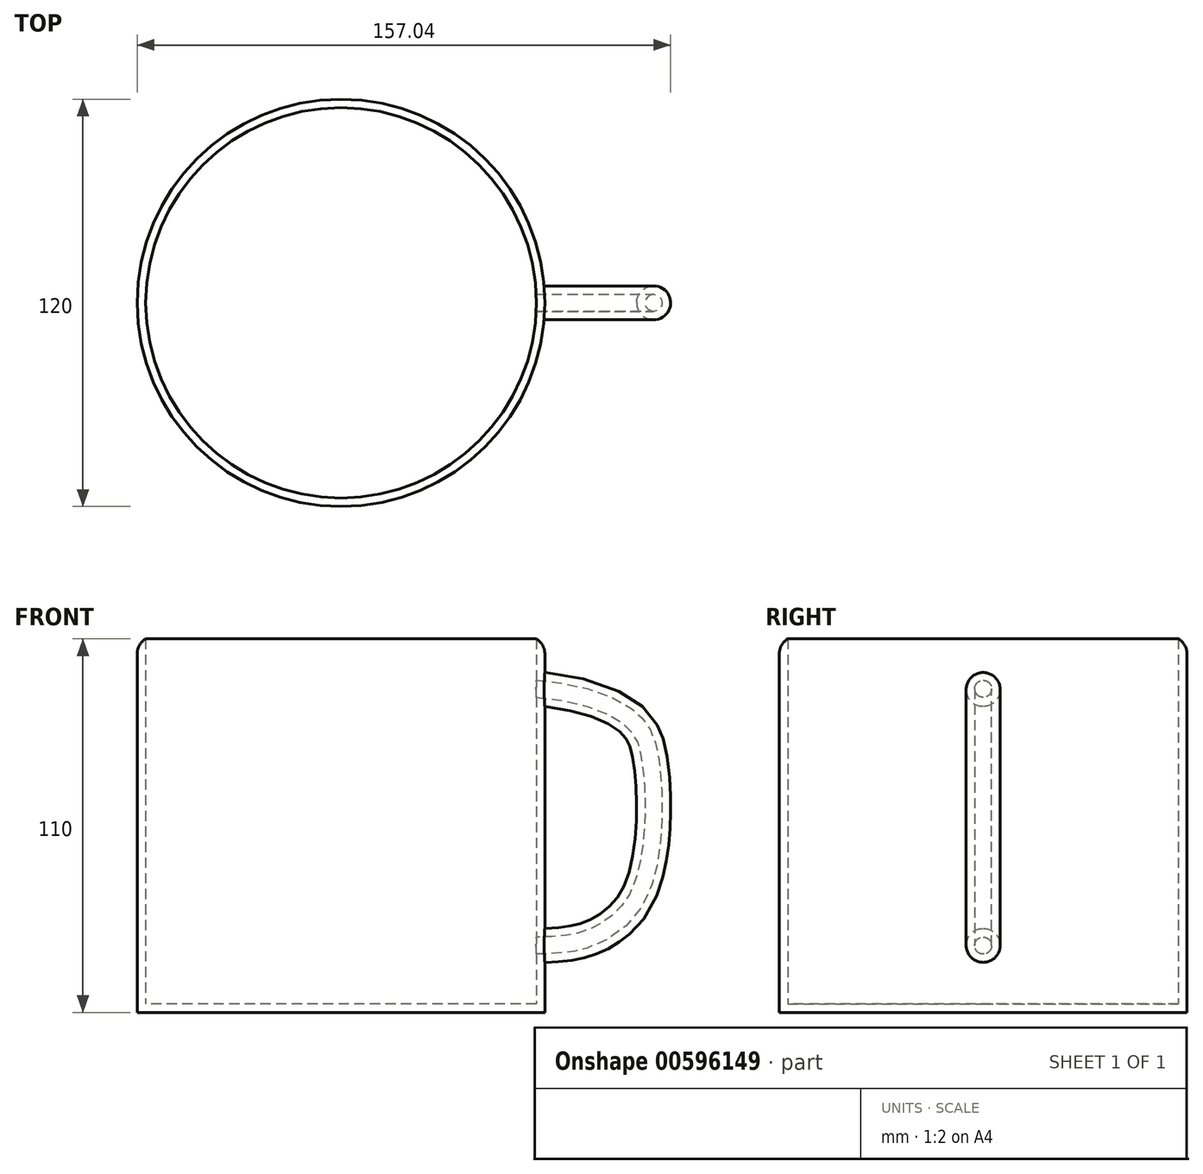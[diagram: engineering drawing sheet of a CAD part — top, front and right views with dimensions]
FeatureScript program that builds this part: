
annotation { "Feature Type Name" : "Feature", "Feature Type Description" : "" }
export const myFeature = defineFeature(function(context is Context, id is Id, definition is map)
    precondition{}
    {
        {
            var Q0;
            Q0=qCreatedBy(makeId("Top.planeOp"),FACE);
            var sketch = newSketch(context, id + "F0", { "sketchPlane" : qUnion([Q0])});
            skCircle(sketch, "E0", {"center": v(0, 0) * mm, "radius": 60 * mm});
            skSolve(sketch);
        }
        {
            var Q0;
            Q0=makeQuery(id+"F0.imprint","IMPRINT",FACE,{"disambiguationData":[TD([[makeQuery(id+"F0.imprint","IMPRINT",EDGE,{"derivedFrom":sQuery(id+"F0.wireOp",EDGE,"E0")}),1.0]])]});
            extrude(context, id + "F1", {"entities" : qUnion([Q0]), "depth" : 110 * mm, "offsetDistance" : 25 * mm});
        }
        {
            var Q0;
            Q0=qCreatedBy(makeId("Right.planeOp"),FACE);
            cPlane(context, id + "F2", {"entities" : qUnion([Q0]), "cplaneType" : CPlaneType.OFFSET, "offset" : 52.9 * mm, "width" : 150 * mm, "height" : 150 * mm});
        }
        {
            var Q0;
            Q0=qCreatedBy(makeId("Front.planeOp"),FACE);
            var sketch = newSketch(context, id + "F3", { "sketchPlane" : qUnion([Q0])});
            skFitSpline(sketch, "E1", {"points": [v(46.24, 96.2) * mm, v(86.06, 86.84) * mm, v(91.82, 74.57) * mm, v(92.58, 53.65) * mm, v(86.94, 31.76) * mm, v(75.03, 21.72) * mm, v(63.63, 19.16) * mm, v(47.33, 19.08) * mm], "startDerivative": vector(266.3, 12.93) * mm, "endDerivative": vector(-113.59, 6.31) * mm});
            skSolve(sketch);
        }
        {
            var Q0;
            Q0=qCreatedBy(id+"F2.planeOp",FACE);
            var sketch = newSketch(context, id + "F4", { "sketchPlane" : qUnion([Q0])});
            skCircle(sketch, "E2", {"center": v(0, 95.52) * mm, "radius": 5 * mm});
            skSolve(sketch);
        }
        {
            var Q0;
            Q0 = qSketchRegion(id + "F4", true);
            var Q1;
            Q1 = qConstructionFilter(qBodyType(qCreatedBy(id + "F3" ,EDGE), BodyType.WIRE), ConstructionObject.NO);
            sweep(context, id + "F5", {"operationType" : NewBodyOperationType.ADD, "profiles" : qUnion([Q0]), "path" : qUnion([Q1])});
        }
        {
            var Q0;
            Q0=makeQuery(id+"F1.opExtrude","CAP_FACE",FACE,{"disambiguationData":[OSD([sQuery(id+"F0.wireOp",EDGE,"E0")])],"isStart":false});
            shell(context, id + "F6", {"entities" : qUnion([Q0]), "thickness" : 2.5 * mm});
        }
        {
            var Q0;
            Q0=makeQuery(id+"F1.opExtrude","CAP_EDGE",EDGE,{"disambiguationData":[OSD([sQuery(id+"F0.wireOp",EDGE,"E0")])],"isStart":false});
            fillet(context, id + "F7", {"entities" : qUnion([Q0]), "radius" : 5 * mm, "tangentPropagation" : true, "allowEdgeOverflow" : false});
        }
    });
